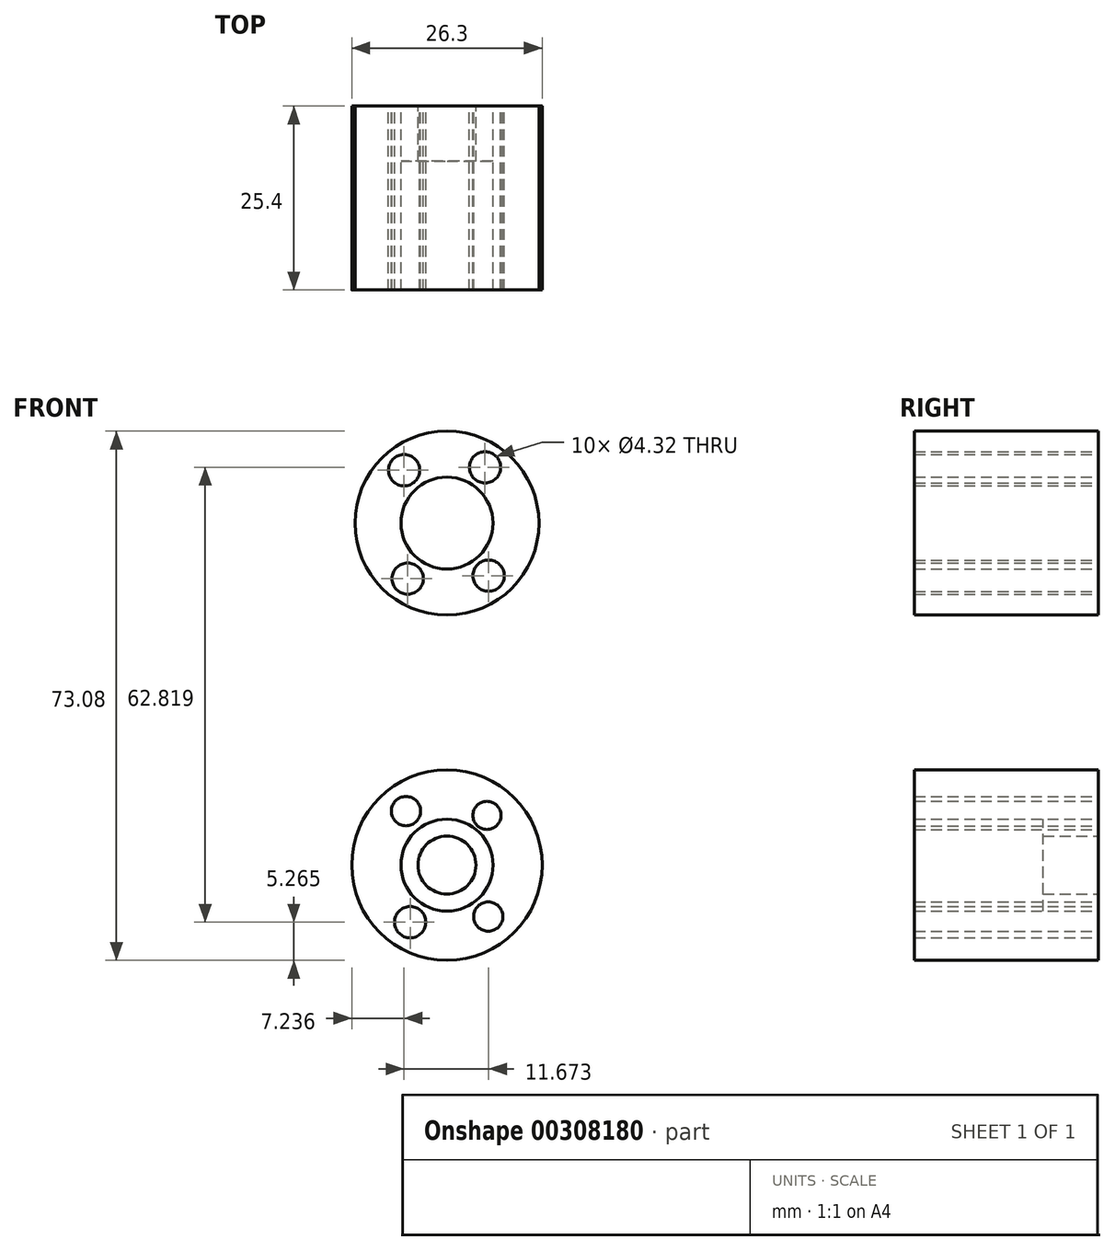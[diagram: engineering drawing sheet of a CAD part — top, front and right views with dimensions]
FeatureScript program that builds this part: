
annotation { "Feature Type Name" : "Feature", "Feature Type Description" : "" }
export const myFeature = defineFeature(function(context is Context, id is Id, definition is map)
    precondition{}
    {
        {
            var Q0;
            Q0=qCreatedBy(makeId("Front.planeOp"),FACE);
            var sketch = newSketch(context, id + "F0", { "sketchPlane" : qUnion([Q0])});
            skCircle(sketch, "E0", {"center": v(0, 0) * mm, "radius": 13.15 * mm});
            skCircle(sketch, "E1", {"center": v(5.52, 6.86) * mm, "radius": 1.94 * mm});
            skCircle(sketch, "E2", {"center": v(5.7, -7.11) * mm, "radius": 2.02 * mm});
            skCircle(sketch, "E3", {"center": v(-5.08, -7.89) * mm, "radius": 2.16 * mm});
            skCircle(sketch, "E4", {"center": v(-5.65, 7.45) * mm, "radius": 2.02 * mm});
            skCircle(sketch, "E5", {"center": v(0, 0) * mm, "radius": 6.35 * mm});
            skCircle(sketch, "E6", {"center": v(0, 0) * mm, "radius": 4 * mm});
            skCircle(sketch, "E7", {"center": v(0, 47.23) * mm, "radius": 12.7 * mm});
            skCircle(sketch, "E8", {"center": v(0, 47.23) * mm, "radius": 6.35 * mm});
            skCircle(sketch, "E9", {"center": v(0, 47.23) * mm, "radius": 4 * mm});
            skCircle(sketch, "E10", {"center": v(-5.91, 54.53) * mm, "radius": 2.16 * mm});
            skCircle(sketch, "E11", {"center": v(5.26, 54.93) * mm, "radius": 2.16 * mm});
            skCircle(sketch, "E12", {"center": v(5.76, 39.97) * mm, "radius": 2.16 * mm});
            skCircle(sketch, "E13", {"center": v(-5.42, 39.56) * mm, "radius": 2.16 * mm});
            skSolve(sketch);
        }
        {
            var Q0;
            Q0=makeQuery(id+"F0.imprint","IMPRINT",FACE,{"disambiguationData":[TD([[makeQuery(id+"F0.imprint","IMPRINT",EDGE,{"derivedFrom":sQuery(id+"F0.wireOp",EDGE,"E5")}),1.0]])]});
            extrude(context, id + "F1", {"entities" : qUnion([Q0]), "depth" : 7.62 * mm});
        }
        {
            var Q0;
            Q0=makeQuery(id+"F0.imprint","IMPRINT",FACE,{"disambiguationData":[TD([[makeQuery(id+"F0.imprint","IMPRINT",EDGE,{"derivedFrom":sQuery(id+"F0.wireOp",EDGE,"E0")}),1.0]])]});
            extrude(context, id + "F2", {"entities" : qUnion([Q0]), "operationType" : NewBodyOperationType.ADD, "depth" : 25.4 * mm});
        }
        {
            var Q0;
            Q0 = qSketchRegion(id + "F0", true);
            extrude(context, id + "F3", {"entities" : qUnion([Q0]), "operationType" : NewBodyOperationType.ADD, "depth" : 25.4 * mm});
        }
        {
            var Q0;
            Q0 = qSketchRegion(id + "F0", true);
            var Q1;
            Q1=makeQuery(id+"F0.imprint","IMPRINT",FACE,{"disambiguationData":[TD([[makeQuery(id+"F0.imprint","IMPRINT",EDGE,{"derivedFrom":sQuery(id+"F0.wireOp",EDGE,"E8")}),1.0]])]});
            var Q2;
            Q2=makeQuery(id+"F0.imprint","IMPRINT",FACE,{"disambiguationData":[TD([[makeQuery(id+"F0.imprint","IMPRINT",EDGE,{"derivedFrom":sQuery(id+"F0.wireOp",EDGE,"E9")}),1.0]])]});
            extrude(context, id + "F4", {"entities" : qUnion([Q0, Q1, Q2]), "depth" : 25.4 * mm});
        }
    });
